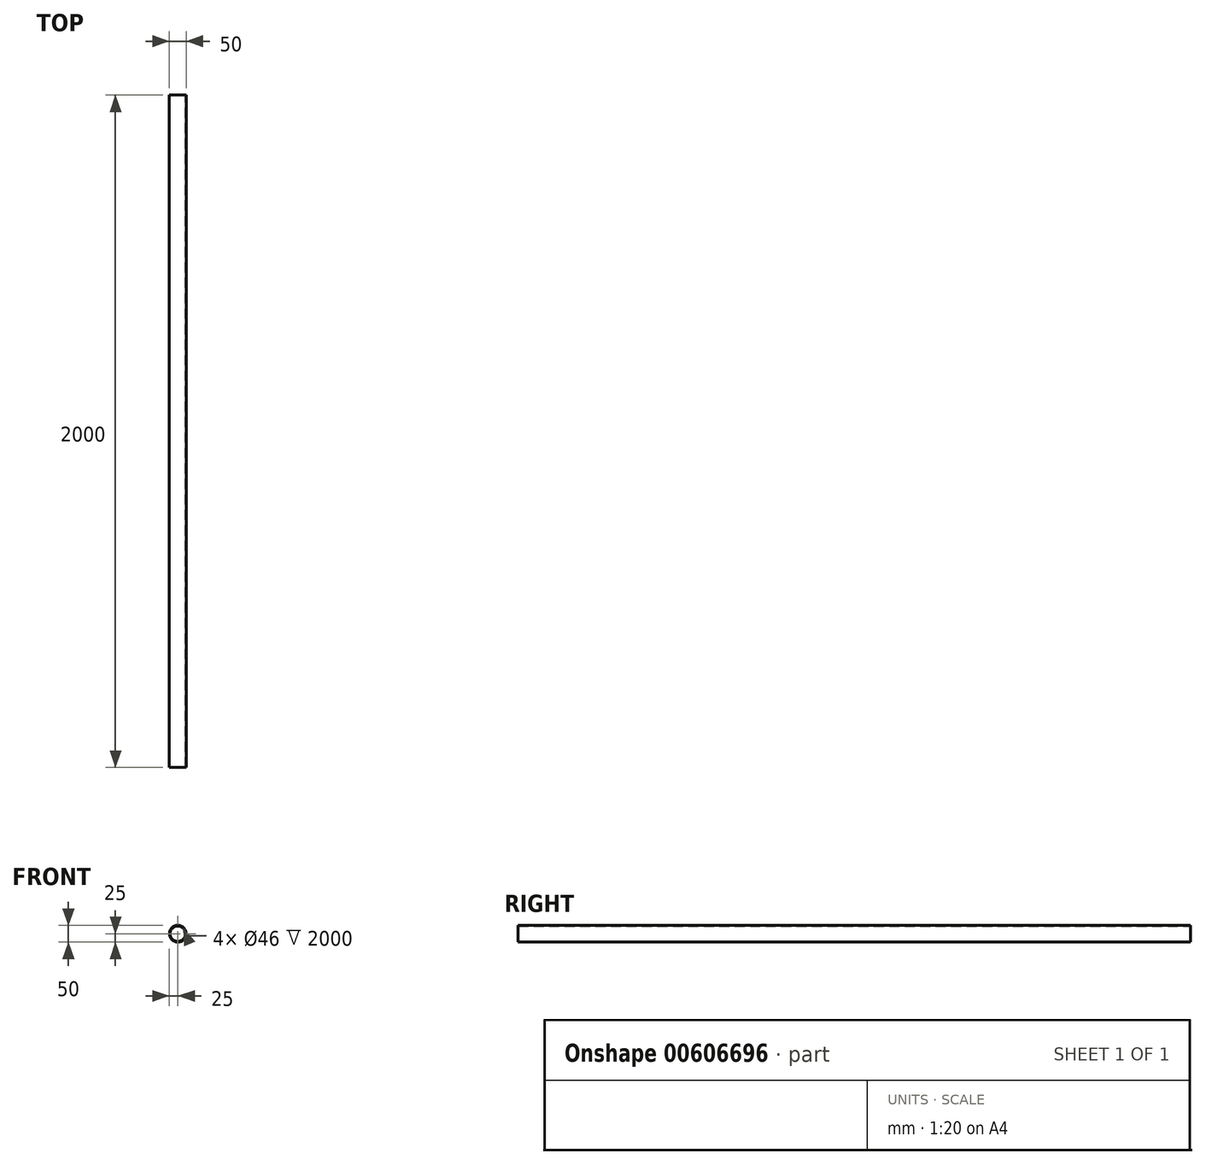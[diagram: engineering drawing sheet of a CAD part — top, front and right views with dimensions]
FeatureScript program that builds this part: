
annotation { "Feature Type Name" : "Feature", "Feature Type Description" : "" }
export const myFeature = defineFeature(function(context is Context, id is Id, definition is map)
    precondition{}
    {
        {
            var Q0;
            Q0=qCreatedBy(makeId("Front.planeOp"),FACE);
            var sketch = newSketch(context, id + "F0", { "sketchPlane" : qUnion([Q0])});
            skCircle(sketch, "E0", {"center": v(0, 0) * mm, "radius": 25 * mm});
            skCircle(sketch, "E1", {"center": v(0, 0) * mm, "radius": 23 * mm});
            skSolve(sketch);
        }
        {
            var Q0;
            Q0 = qSketchRegion(id + "F0", true);
            extrude(context, id + "F1", {"entities" : qUnion([Q0]), "depth" : 2000 * mm, "offsetDistance" : 25 * mm});
        }
    });
